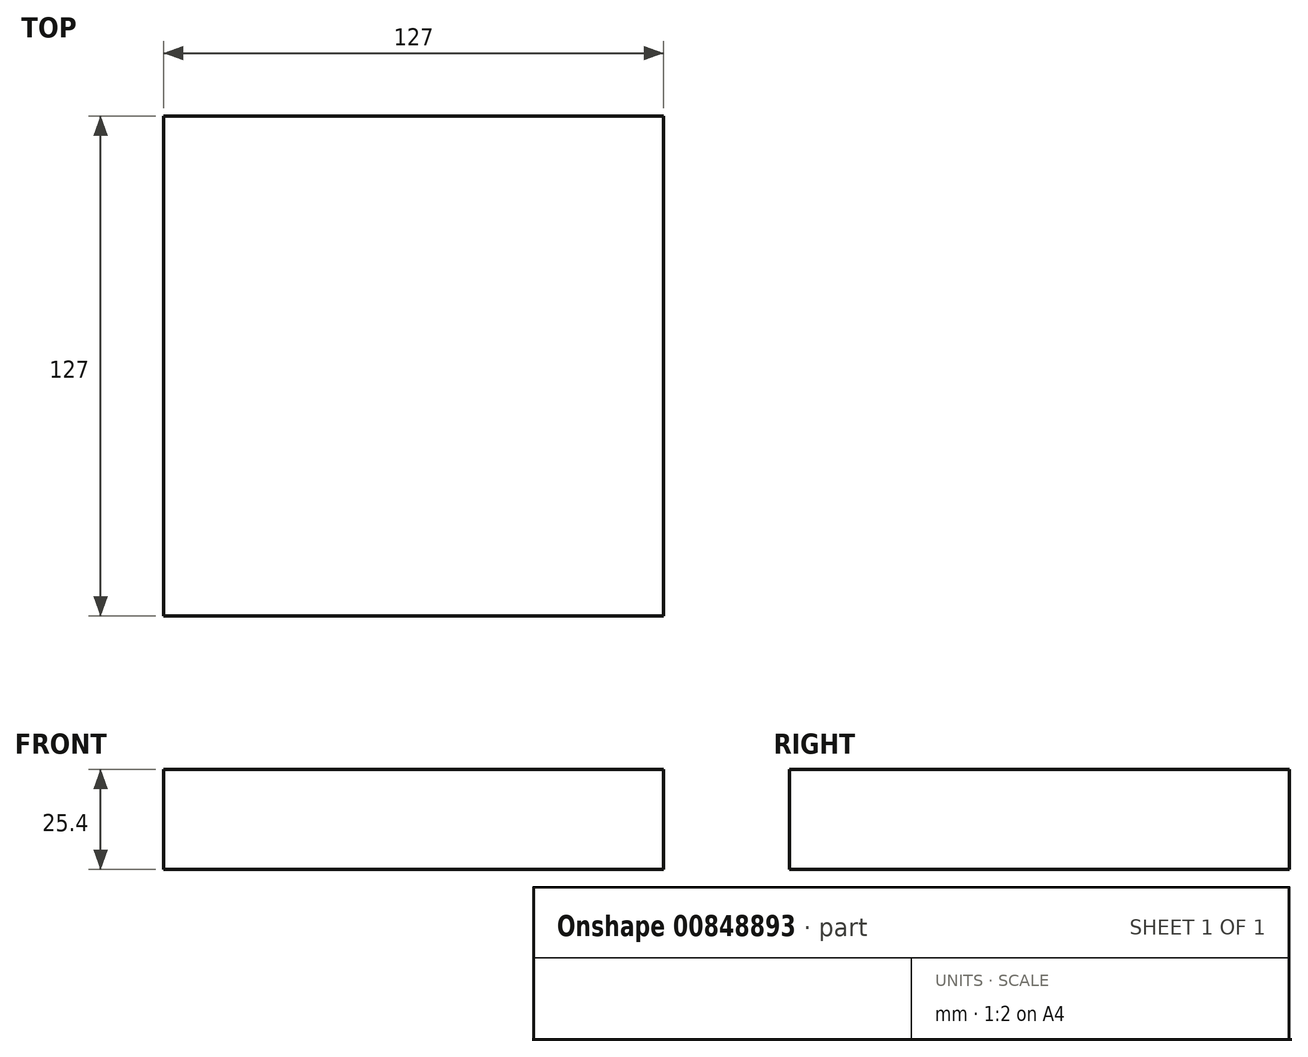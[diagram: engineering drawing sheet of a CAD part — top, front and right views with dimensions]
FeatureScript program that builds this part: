
annotation { "Feature Type Name" : "Feature", "Feature Type Description" : "" }
export const myFeature = defineFeature(function(context is Context, id is Id, definition is map)
    precondition{}
    {
        {
            var Q0;
            Q0=qCreatedBy(makeId("Top.planeOp"),FACE);
            var sketch = newSketch(context, id + "F0", { "sketchPlane" : qUnion([Q0])});
            skLineSegment(sketch, "E0.bottom", {"start": v(-63.5, 63.5) * mm, "end": v(63.5, 63.5) * mm});
            skLineSegment(sketch, "E0.top", {"start": v(-63.5, -63.5) * mm, "end": v(63.5, -63.5) * mm});
            skLineSegment(sketch, "E0.left", {"start": v(-63.5, 63.5) * mm, "end": v(-63.5, -63.5) * mm});
            skLineSegment(sketch, "E0.right", {"start": v(63.5, 63.5) * mm, "end": v(63.5, -63.5) * mm});
            skPoint(sketch, "E0.middle", {"position": v(0, 0) * mm});
            skSolve(sketch);
        }
        {
            var Q0;
            Q0=makeQuery(id+"F0.imprint","IMPRINT",FACE,{"disambiguationData":[TD([[makeQuery(id+"F0.imprint","IMPRINT",EDGE,{"derivedFrom":sQuery(id+"F0.wireOp",EDGE,"E0.bottom")}),-1.0]])]});
            extrude(context, id + "F1", {"entities" : qUnion([Q0]), "endBound" : BoundingType.SYMMETRIC, "depth" : 25.4 * mm, "offsetDistance" : 25.4 * mm});
        }
    });
